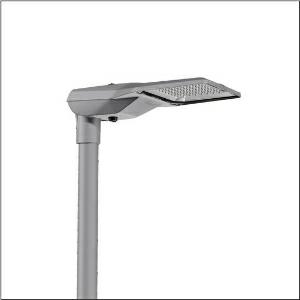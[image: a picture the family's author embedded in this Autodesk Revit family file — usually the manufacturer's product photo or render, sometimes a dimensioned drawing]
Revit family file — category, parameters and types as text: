
# Revit family: streetlight_sl_21_midi___p0_5a_5xe3v33t08lb_b8c4
name_source: partatom
category: Lighting Fixtures
units: mm (PartAtom-declared; Revit-internal decimal feet)

## family parameters
Cut with Voids When Loaded = No
Host = Face
Light Source = No
Part Type = Normal
Room Calculation Point = No
Round Connector Dimension = Use Diameter
Shared = No

## types (1)
- --- (1 x LED, 14100 lm, 99.6 W, 3000K)
    Apparent Load = 100 VA
    CIE Flux Codes = 37 73 96 100 100
    Color Rendering = 70
    Color Temperature = 3000K
    Default Elevation = 1800 mm
    Description = Streetlight SL 21 midi, mast luminaire, primary light control with lens, of PMMA, primary optical cover: cover, of toughened safety glass, transparent, light distribution: P0.5a, light emission: direct distribution, primary light characteristic: asymmetric, installation type: post-top, side-entry, LED, High Power LED, rated luminous flux: 14.100lm, luminous efficacy: 142lm/W, light colour: 730, colour temperature: 3000K, control gear: D4i, control: pre-setting: logarithmic dimming characteristic, flexible luminous flux parameterisation, time-dependent luminous flux control, constant luminous flux control, overheat protection, mains connection: 230..240V, AC, 50/60Hz, start of lifetime: 100W, end of service life: 102W, reduction: 46W, luminaire housing, of diecast aluminium, powder-coated, SITECO metallic grey (DB 702S), corrosivity category C5 high according to DIN EN ISO 12944, multi-level sealing system, sealing non-destructively replaceable, inclination adjustable: 0°, 5°, 10°, 15°, please order mast flange separately, length: 644mm, width: 335mm, height: 110mm, mast flange for spigot size: 42mm (side-entry): 5XC10008XM4, 60/48mm (side-entry/post-top): 5XC10108XM2, 76/60mm (side-entry/post-top): 5XC10108XM1, mounting height: 4..8m, Smart Interface below and above, protection rating (complete): IP66, insulation class (complete): insulation class II (safety insulation), certification: CE, ENEC, ENEC+, VDE, impact resistance: IK10, permissible operating ambient temperature for outdoor applications: -40..+50°C, standard-compliant lighting for roads and squares, packaging unit: 1 piece

Light Distribution: P0.5a
    Height = 111 mm
    Lamp = 1 x LED
    Lamp Light Flux = 14100 lm
    Lamp Power = 99.6 W
    Lamp count = 1
    Length = 644 mm
    Luminous efficacy = 142 lm/W
    Manufacturer = Siteco
    ModVariant = No
    Model = 5XE3V33T08LB
    Number of Poles = 1
    OnlyDefault = Yes
    Power Factor = 1
    Product Name = Streetlight SL 21 midi | P0.5a
    Product group = mast luminaire | pylon top
    ProductGroupID = 6100
    Protection Class = Protection class II
    Protection Degree = IP 66
    RLX_Detail_Level = 1
    RLX_Emergency_Light_Flux = 0 lm
    RLX_Emergency_Type = 0
    RLX_Emergency_Type_DB = No
    RlxData = <blob elided: 26477 chars, md5=56ac0d4a>
    Socket = socket
    Standby Power = 0 W
    System Light Flux = 14100 lm
    System Power = 100 W
    Type Comments = factory setting: luminous flux: 100 % | dim-lin: 254 | 1020 mA
    Type Image = l_1004304.jpg
    URL = http://relux.com
    VarID = @adj_032811
    Voltage = 0 V
    Weight = 0.00 kg
    Width = 336 mm

## geometry (parser evidence)
native form markers: Blend x4, Sweep x12
no freeform markers — native parametric forms only
